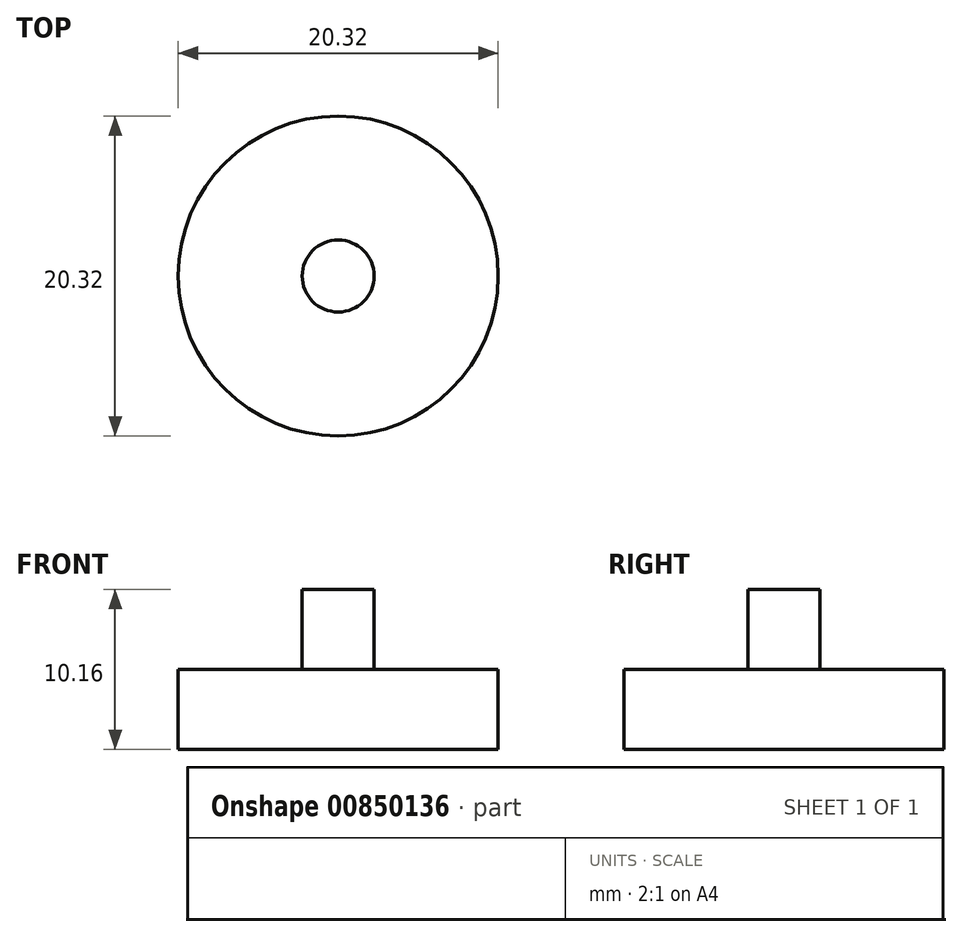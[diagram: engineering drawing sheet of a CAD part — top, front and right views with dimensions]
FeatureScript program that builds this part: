
annotation { "Feature Type Name" : "Feature", "Feature Type Description" : "" }
export const myFeature = defineFeature(function(context is Context, id is Id, definition is map)
    precondition{}
    {
        {
            var Q0;
            Q0=qCreatedBy(makeId("Top.planeOp"),FACE);
            var sketch = newSketch(context, id + "F0", { "sketchPlane" : qUnion([Q0])});
            skCircle(sketch, "E0", {"center": v(0, 0) * mm, "radius": 2.29 * mm});
            skSolve(sketch);
        }
        {
            var Q0;
            Q0 = qSketchRegion(id + "F0", true);
            extrude(context, id + "F1", {"entities" : qUnion([Q0]), "depth" : 5.08 * mm, "offsetDistance" : 25.4 * mm});
        }
        {
            var Q0;
            Q0=makeQuery(id+"F1.opExtrude","CAP_FACE",FACE,{"disambiguationData":[OSD([sQuery(id+"F0.wireOp",EDGE,"E0")])],"isStart":true});
            var sketch = newSketch(context, id + "F2", { "sketchPlane" : qUnion([Q0])});
            skCircle(sketch, "E1", {"center": v(0, 0) * mm, "radius": 10.16 * mm});
            skSolve(sketch);
        }
        {
            var Q0;
            Q0=makeQuery(id+"F2.imprint","IMPRINT",FACE,{"disambiguationData":[TD([[makeQuery(id+"F2.imprint","IMPRINT",EDGE,{"derivedFrom":sQuery(id+"F2.wireOp",EDGE,"E1")}),1.0]])]});
            var Q1;
            Q1=makeQuery(id+"F2.imprint","IMPRINT",FACE,{"disambiguationData":[TD([[makeQuery(id+"F2.imprint","IMPRINT",EDGE,{"derivedFrom":makeQuery(id+"F1.opExtrude","CAP_EDGE",EDGE,{"disambiguationData":[OSD([sQuery(id+"F0.wireOp",EDGE,"E0")])],"isStart":true})}),-1.0]])]});
            extrude(context, id + "F3", {"entities" : qUnion([Q0, Q1]), "operationType" : NewBodyOperationType.ADD, "depth" : 5.08 * mm, "offsetDistance" : 25.4 * mm});
        }
    });
